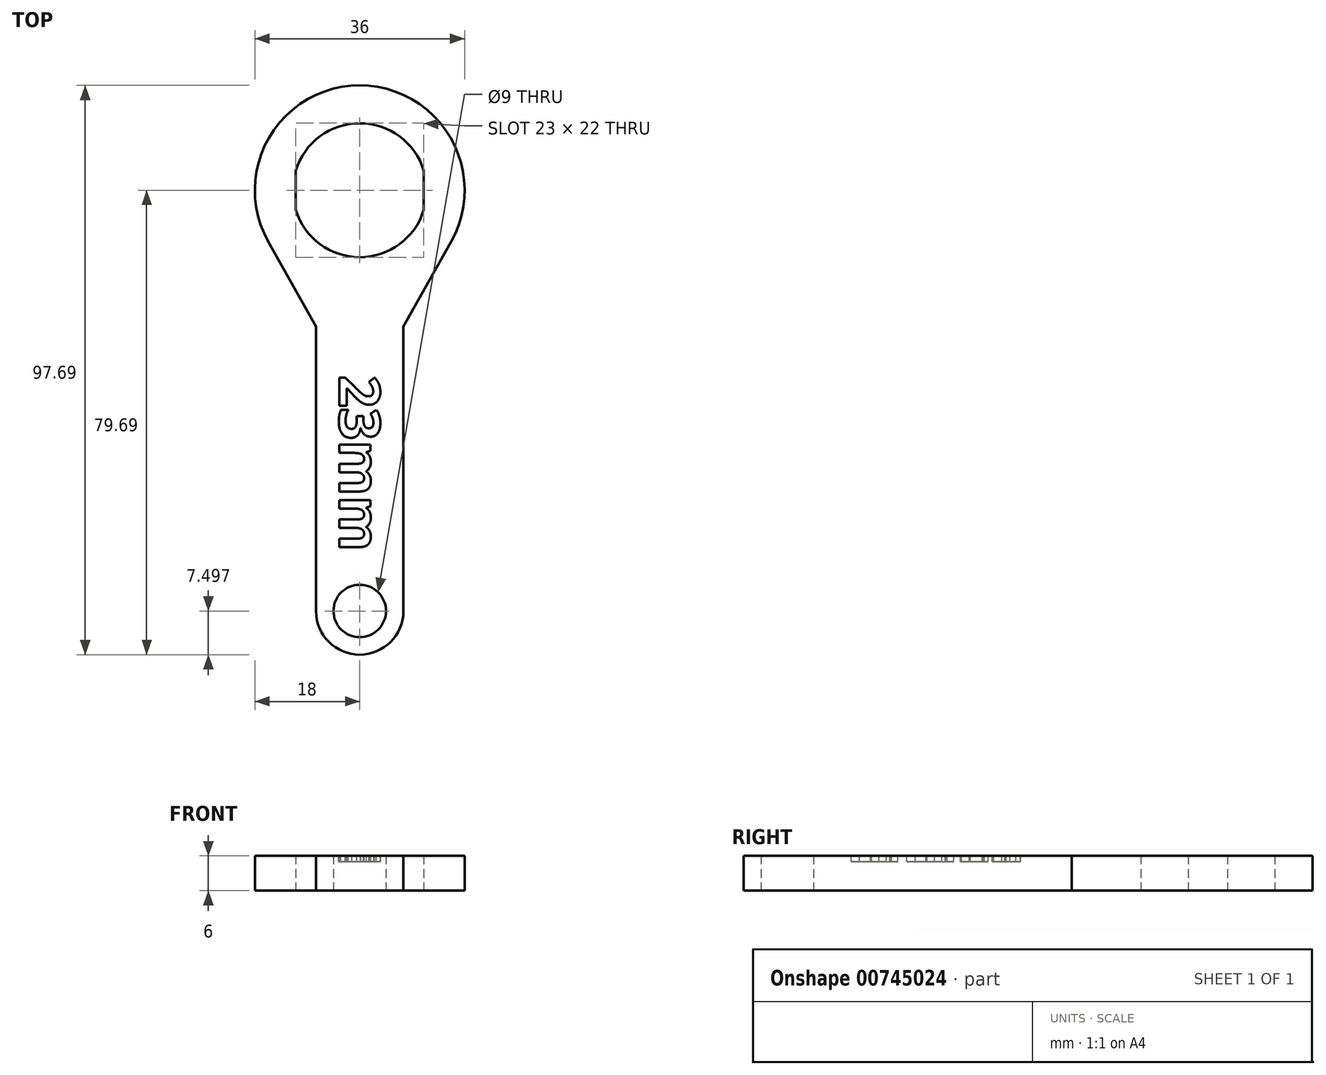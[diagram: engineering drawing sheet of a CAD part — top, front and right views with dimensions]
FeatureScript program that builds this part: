
annotation { "Feature Type Name" : "Feature", "Feature Type Description" : "" }
export const myFeature = defineFeature(function(context is Context, id is Id, definition is map)
    precondition{}
    {
        {
            var Q0;
            Q0=qCreatedBy(makeId("Top.planeOp"),FACE);
            var sketch = newSketch(context, id + "F0", { "sketchPlane" : qUnion([Q0])});
            skArc(sketch, "E0", {"start": v(-11, -3.35) * mm, "mid": v(0, -11.5) * mm, "end": v(11, -3.35) * mm});
            skLineSegment(sketch, "E1.left", {"start": v(11, -3.35) * mm, "end": v(11, 3.35) * mm});
            skLineSegment(sketch, "E1.right", {"start": v(-11, -3.35) * mm, "end": v(-11, 3.35) * mm});
            skArc(sketch, "E2.trimOffspring", {"start": v(11, 3.35) * mm, "mid": v(0, 11.5) * mm, "end": v(-11, 3.35) * mm});
            skArc(sketch, "E3", {"start": v(15.68, -8.83) * mm, "mid": v(0, 18) * mm, "end": v(-15.68, -8.83) * mm});
            skLineSegment(sketch, "E4.bottom", {"start": v(0, -79.7) * mm, "end": v(0, -79.7) * mm});
            skLineSegment(sketch, "E4.left", {"start": v(7.5, -72.2) * mm, "end": v(7.5, -23.36) * mm});
            skLineSegment(sketch, "E4.right", {"start": v(-7.5, -72.2) * mm, "end": v(-7.5, -23.36) * mm});
            skPoint(sketch, "E4.middle", {"position": v(0, -47.2) * mm});
            skPoint(sketch, "E5.visualSharp", {"position": v(-7.5, -79.7) * mm});
            skArc(sketch, "E5.filletArc", {"start": v(-7.5, -72.2) * mm, "mid": v(-5.3, -77.5) * mm, "end": v(0, -79.7) * mm});
            skPoint(sketch, "E6.visualSharp", {"position": v(7.5, -79.7) * mm});
            skArc(sketch, "E6.filletArc", {"start": v(0, -79.7) * mm, "mid": v(5.3, -77.5) * mm, "end": v(7.5, -72.2) * mm});
            skCircle(sketch, "E7", {"center": v(0, -72.2) * mm, "radius": 4.5 * mm});
            skLineSegment(sketch, "E8", {"start": v(-7.5, -23.36) * mm, "end": v(-15.68, -8.83) * mm});
            skLineSegment(sketch, "E9.MirrorCS", {"start": v(7.5, -23.36) * mm, "end": v(15.68, -8.83) * mm});
            skSolve(sketch);
        }
        {
            var Q0;
            Q0=makeQuery(id+"F0.imprint","IMPRINT",FACE,{"disambiguationData":[TD([[makeQuery(id+"F0.imprint","IMPRINT",EDGE,{"derivedFrom":sQuery(id+"F0.wireOp",EDGE,"E0")}),-1.0]])]});
            extrude(context, id + "F1", {"entities" : qUnion([Q0]), "depth" : 6 * mm, "offsetDistance" : 25 * mm});
        }
        {
            var Q0;
            Q0=makeQuery(id+"F1.opExtrude","CAP_FACE",FACE,{"disambiguationData":[OSD([sQuery(id+"F0.wireOp",EDGE,"E0"),sQuery(id+"F0.wireOp",EDGE,"E1.left"),sQuery(id+"F0.wireOp",EDGE,"E1.right"),sQuery(id+"F0.wireOp",EDGE,"E2.trimOffspring"),sQuery(id+"F0.wireOp",EDGE,"E3"),sQuery(id+"F0.wireOp",EDGE,"E4.left"),sQuery(id+"F0.wireOp",EDGE,"E4.right"),sQuery(id+"F0.wireOp",EDGE,"E5.filletArc"),sQuery(id+"F0.wireOp",EDGE,"E6.filletArc"),sQuery(id+"F0.wireOp",EDGE,"E7"),sQuery(id+"F0.wireOp",EDGE,"E8"),sQuery(id+"F0.wireOp",EDGE,"E9.MirrorCS")])],"isStart":false});
            var sketch = newSketch(context, id + "F2", { "sketchPlane" : qUnion([Q0])});
            skText(sketch, "E10", { "text": "23mm", "fontName": "OpenSans-Bold.ttf"});
            const initialGuessF2  = {"E10": [-0.0035, -0.03177, 0, -1, 0.007]};
            skSetInitialGuess(sketch, initialGuessF2);
            skSolve(sketch);
        }
        {
            var Q0;
            Q0 = qSketchRegion(id + "F2", true);
            extrude(context, id + "F3", {"entities" : qUnion([Q0]), "operationType" : NewBodyOperationType.REMOVE, "oppositeDirection" : true, "depth" : 1 * mm, "offsetDistance" : 25 * mm});
        }
    });
